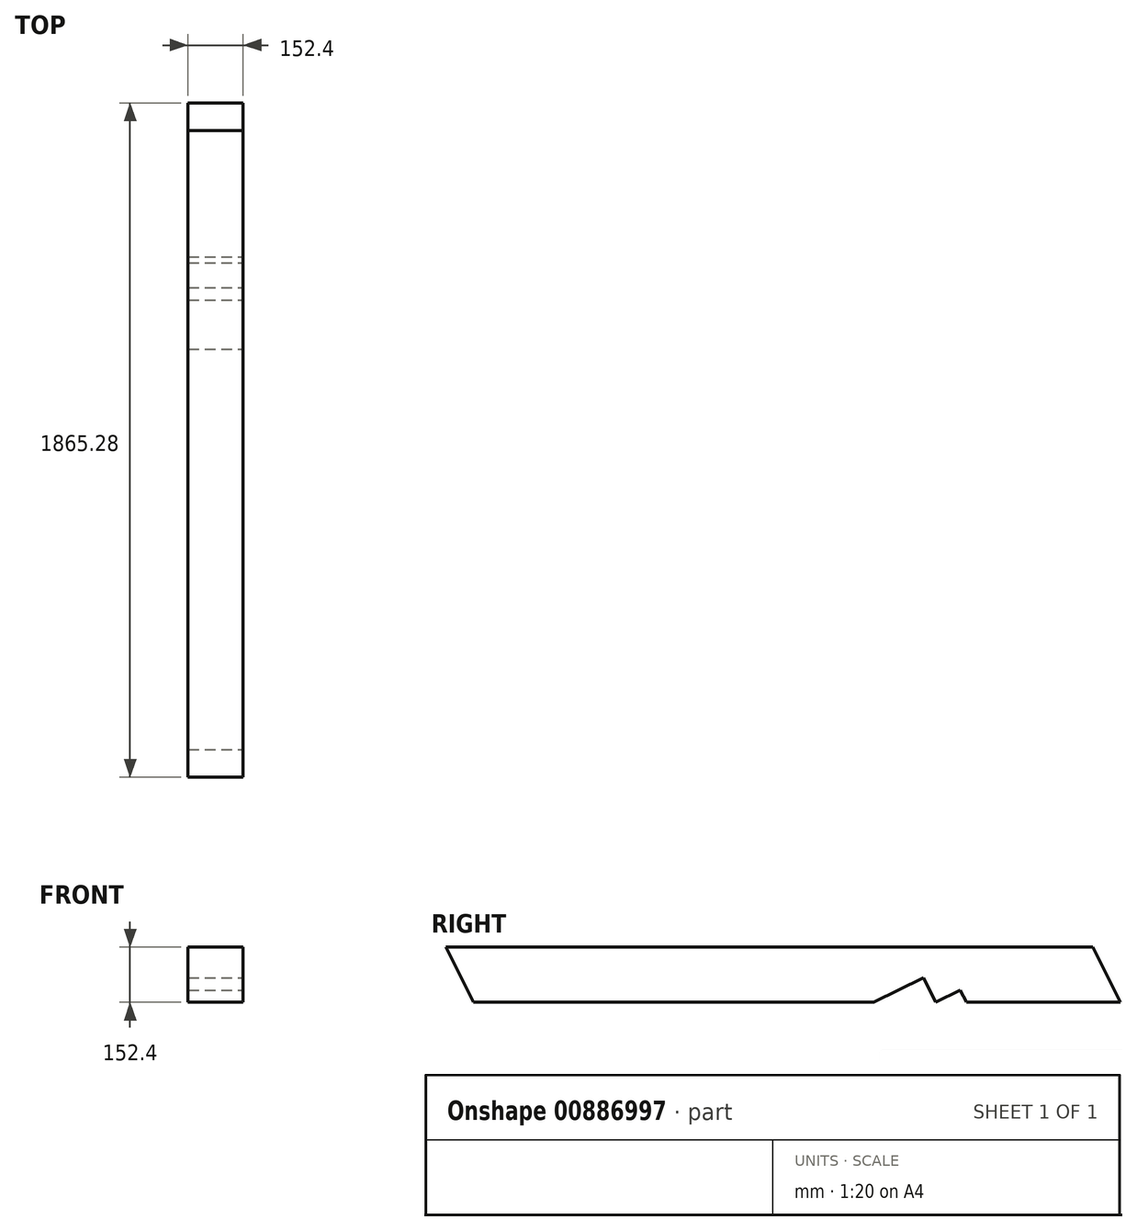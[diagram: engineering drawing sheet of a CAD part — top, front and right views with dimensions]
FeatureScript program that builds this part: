
annotation { "Feature Type Name" : "Feature", "Feature Type Description" : "" }
export const myFeature = defineFeature(function(context is Context, id is Id, definition is map)
    precondition{}
    {
        {
            var Q0;
            Q0=qCreatedBy(makeId("Front.planeOp"),FACE);
            var sketch = newSketch(context, id + "F0", { "sketchPlane" : qUnion([Q0])});
            skLineSegment(sketch, "E0.bottom", {"start": v(0, 0) * mm, "end": v(152.4, 0) * mm});
            skLineSegment(sketch, "E0.top", {"start": v(0, 152.4) * mm, "end": v(152.4, 152.4) * mm});
            skLineSegment(sketch, "E0.left", {"start": v(0, 0) * mm, "end": v(0, 152.4) * mm});
            skLineSegment(sketch, "E0.right", {"start": v(152.4, 0) * mm, "end": v(152.4, 152.4) * mm});
            skSolve(sketch);
        }
        {
            var Q0;
            Q0 = qSketchRegion(id + "F0", true);
            extrude(context, id + "F1", {"entities" : qUnion([Q0]), "depth" : 3048 * mm, "offsetDistance" : 25.4 * mm});
        }
        {
            var Q0;
            Q0=makeQuery(id+"F1.opExtrude","SWEPT_FACE",FACE,{"disambiguationData":[OSD([sQuery(id+"F0.wireOp",EDGE,"E0.right")])]});
            var sketch = newSketch(context, id + "F2", { "sketchPlane" : qUnion([Q0])});
            skLineSegment(sketch, "E1", {"start": v(-3048, 152.4) * mm, "end": v(-2971.8, 0) * mm});
            skLineSegment(sketch, "E2", {"start": v(-2971.8, 0) * mm, "end": v(-3048, 0) * mm});
            skLineSegment(sketch, "E3", {"start": v(-3048, 0) * mm, "end": v(-3048, 152.4) * mm});
            skLineSegment(sketch, "E4", {"start": v(-1258.92, 152.4) * mm, "end": v(-1182.72, 0) * mm});
            skLineSegment(sketch, "E5", {"start": v(0, 152.4) * mm, "end": v(-1258.92, 152.4) * mm});
            skLineSegment(sketch, "E6", {"start": v(-1608.7, 0) * mm, "end": v(-1625.73, 34.08) * mm});
            skLineSegment(sketch, "E7", {"start": v(-1625.73, 34.08) * mm, "end": v(-1693.89, 0) * mm});
            skLineSegment(sketch, "E8", {"start": v(-1693.89, 0) * mm, "end": v(-1727.96, 68.16) * mm});
            skLineSegment(sketch, "E9", {"start": v(-1727.96, 68.16) * mm, "end": v(-1864.28, 0) * mm});
            skLineSegment(sketch, "E10", {"start": v(-1864.28, 0) * mm, "end": v(-1693.89, 0) * mm});
            skLineSegment(sketch, "E11", {"start": v(-1608.7, 0) * mm, "end": v(-1693.89, 0) * mm});
            skLineSegment(sketch, "E12", {"start": v(-1182.72, 0) * mm, "end": v(0, 0) * mm});
            skLineSegment(sketch, "E13", {"start": v(0, 0) * mm, "end": v(0, 152.4) * mm});
            skSolve(sketch);
        }
        {
            var Q0;
            Q0 = qSketchRegion(id + "F2", true);
            extrude(context, id + "F3", {"entities" : qUnion([Q0]), "operationType" : NewBodyOperationType.REMOVE, "endBound" : BoundingType.THROUGH_ALL, "oppositeDirection" : true, "depth" : 25.4 * mm, "offsetDistance" : 25.4 * mm});
        }
    });
